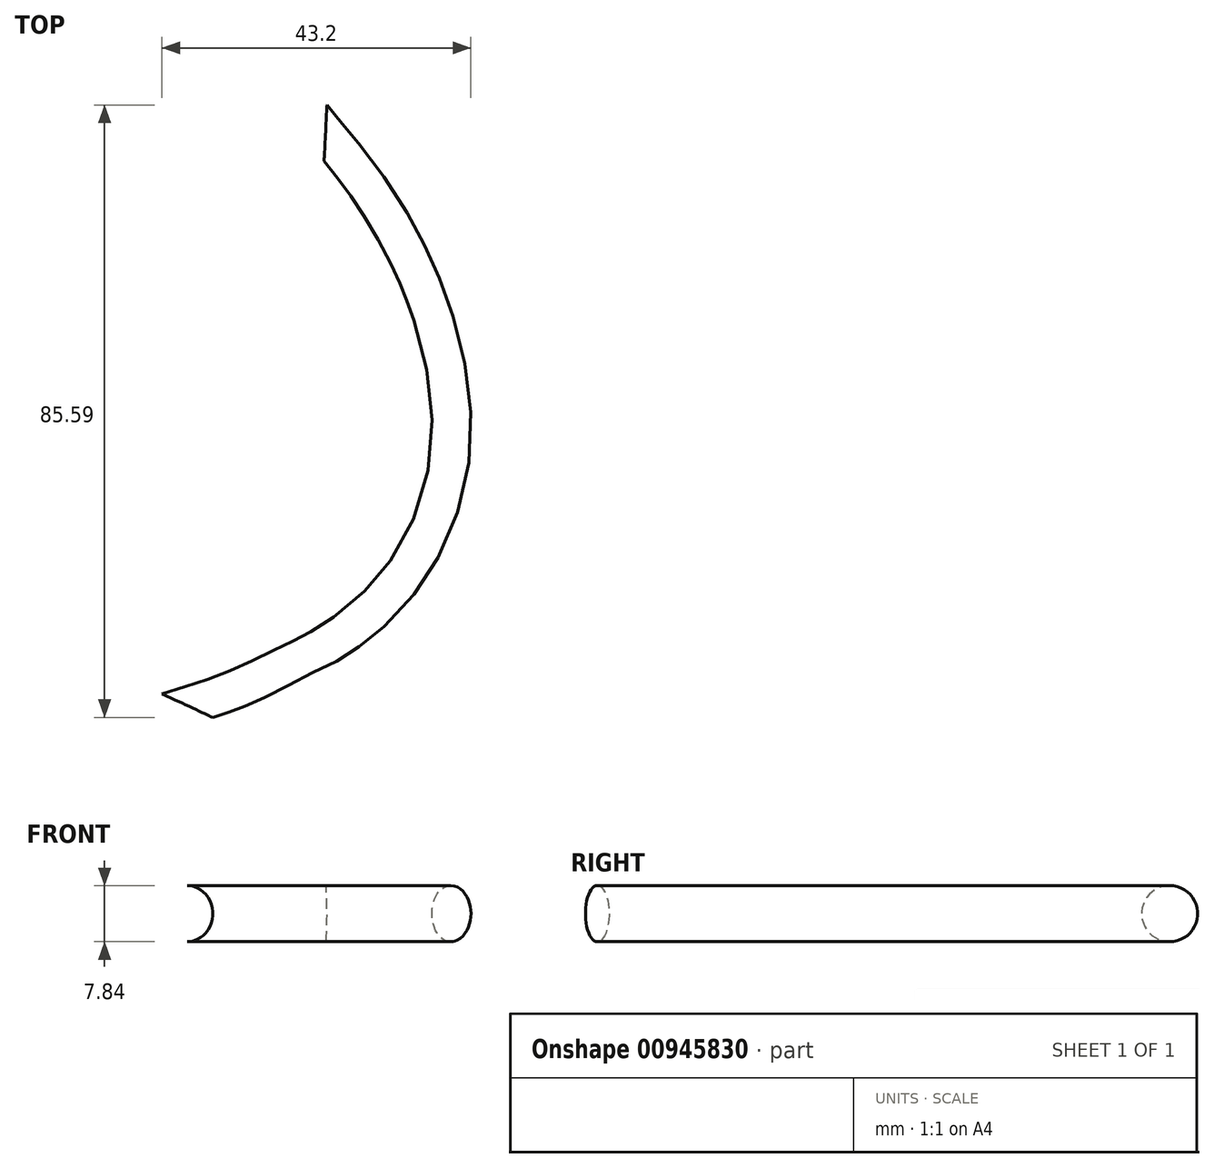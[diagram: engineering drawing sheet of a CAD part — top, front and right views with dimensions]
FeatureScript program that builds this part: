
annotation { "Feature Type Name" : "Feature", "Feature Type Description" : "" }
export const myFeature = defineFeature(function(context is Context, id is Id, definition is map)
    precondition{}
    {
        {
            var Q0;
            Q0=qCreatedBy(makeId("Front.planeOp"),FACE);
            var sketch = newSketch(context, id + "F0", { "sketchPlane" : qUnion([Q0])});
            skCircle(sketch, "E0", {"center": v(-111.15, 31.36) * mm, "radius": 3.92 * mm});
            skSolve(sketch);
        }
        {
            var Q0;
            Q0=qCreatedBy(makeId("Top.planeOp"),FACE);
            var sketch = newSketch(context, id + "F1", { "sketchPlane" : qUnion([Q0])});
            skFitSpline(sketch, "E1", {"points": [v(-139.67, 46.8) * mm, v(-132.62, 36.3) * mm, v(-130, 22.6) * mm, v(-135.63, 18.01) * mm, v(-141.87, 15.07) * mm, v(-147.42, 13.2) * mm], "startDerivative": vector(31.6, -39.26) * mm, "endDerivative": vector(-34.38, -10.4) * mm});
            skSolve(sketch);
        }
        {
            var Q0;
            Q0=makeQuery(id+"F0.imprint","IMPRINT",FACE,{"disambiguationData":[TD([[makeQuery(id+"F0.imprint","IMPRINT",EDGE,{"derivedFrom":sQuery(id+"F0.wireOp",EDGE,"E0")}),1.0]])]});
            var Q1;
            Q1=sQuery(id+"F1.wireOp",EDGE,"E1");
            sweep(context, id + "F2", {"profiles" : qUnion([Q0]), "path" : qUnion([Q1])});
        }
    });
